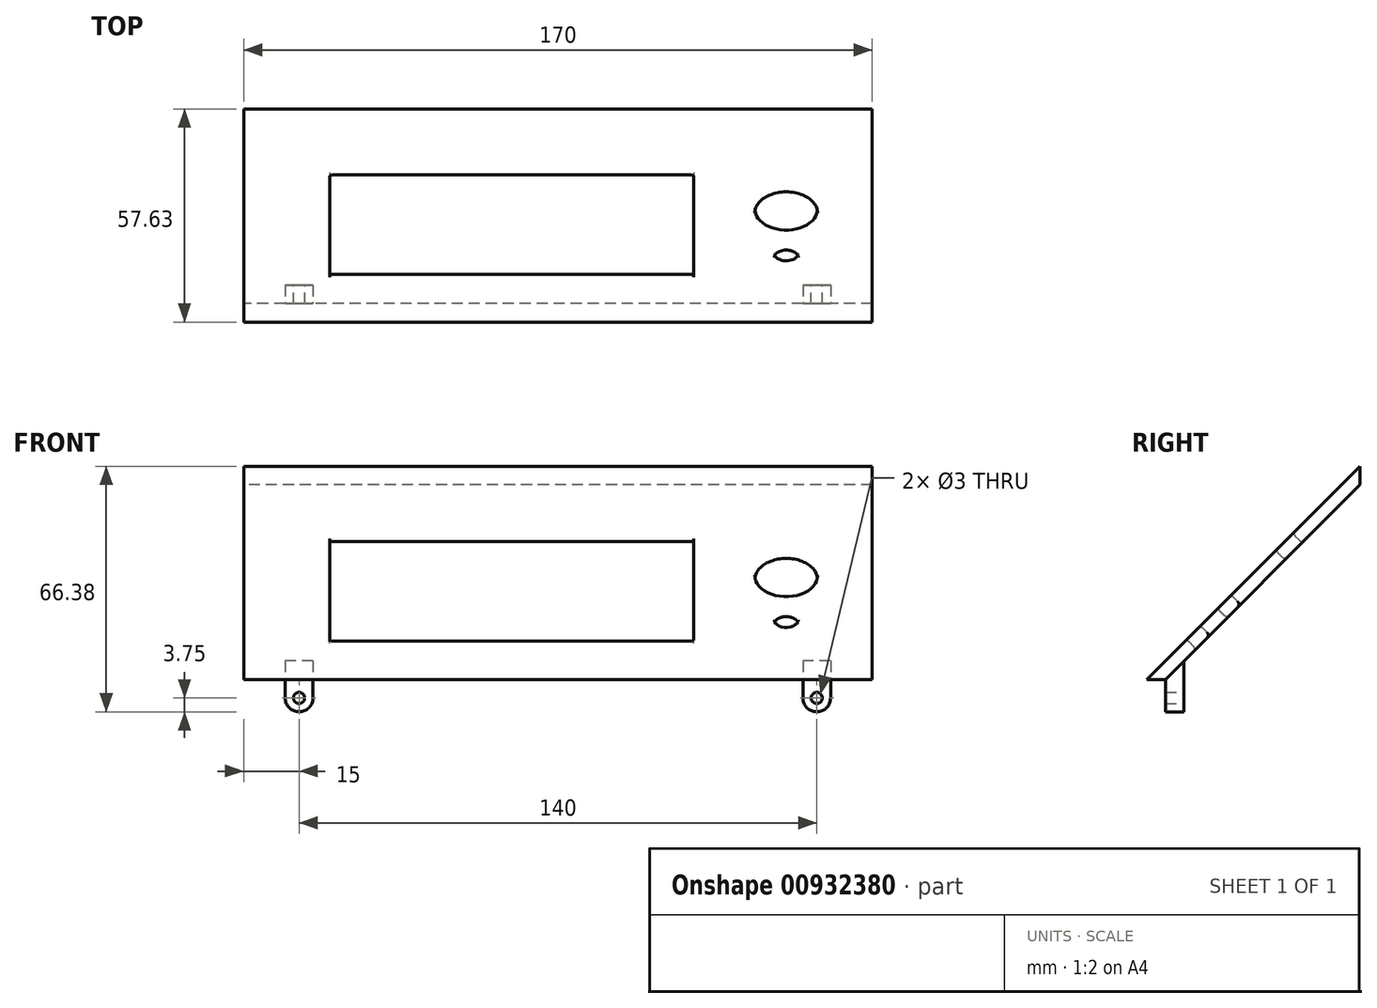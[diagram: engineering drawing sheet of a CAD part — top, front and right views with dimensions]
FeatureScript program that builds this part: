
annotation { "Feature Type Name" : "Feature", "Feature Type Description" : "" }
export const myFeature = defineFeature(function(context is Context, id is Id, definition is map)
    precondition{}
    {
        {
            var Q0;
            Q0=qCreatedBy(makeId("Right.planeOp"),FACE);
            var sketch = newSketch(context, id + "F0", { "sketchPlane" : qUnion([Q0])});
            skLineSegment(sketch, "E0", {"start": v(0, 0) * mm, "end": v(0, 57.63) * mm});
            skLineSegment(sketch, "E1", {"start": v(0, 57.63) * mm, "end": v(57.63, 57.63) * mm});
            skLineSegment(sketch, "E2", {"start": v(57.63, 57.63) * mm, "end": v(0, 0) * mm});
            skLineSegment(sketch, "E3", {"start": v(57.63, 57.63) * mm, "end": v(57.63, 52.63) * mm});
            skLineSegment(sketch, "E4", {"start": v(57.63, 52.63) * mm, "end": v(5, 0) * mm});
            skLineSegment(sketch, "E5", {"start": v(5, 0) * mm, "end": v(0, 0) * mm});
            skSolve(sketch);
        }
        {
            var Q0;
            Q0=makeQuery(id+"F0.imprint","IMPRINT",FACE,{"disambiguationData":[TD([[makeQuery(id+"F0.imprint","IMPRINT",EDGE,{"derivedFrom":sQuery(id+"F0.wireOp",EDGE,"E2")}),1.0]])]});
            extrude(context, id + "F1", {"entities" : qUnion([Q0]), "depth" : 85 * mm, "offsetDistance" : 25 * mm, "hasSecondDirection" : true, "secondDirectionOppositeDirection" : true, "secondDirectionDepth" : 85 * mm});
        }
        {
            var Q0;
            Q0=makeQuery(id+"F1.opExtrude","SWEPT_FACE",FACE,{"disambiguationData":[OSD([sQuery(id+"F0.wireOp",EDGE,"E2")])]});
            var sketch = newSketch(context, id + "F2", { "sketchPlane" : qUnion([Q0])});
            skLineSegment(sketch, "E6.bottom", {"start": v(-61.75, 55.75) * mm, "end": v(36.75, 55.75) * mm});
            skLineSegment(sketch, "E6.top", {"start": v(-61.75, 15.25) * mm, "end": v(36.75, 15.25) * mm});
            skLineSegment(sketch, "E6.left", {"start": v(-61.75, 55.75) * mm, "end": v(-61.75, 15.25) * mm});
            skLineSegment(sketch, "E6.right", {"start": v(36.75, 55.75) * mm, "end": v(36.75, 15.25) * mm});
            skCircle(sketch, "E7", {"center": v(61.75, 40.75) * mm, "radius": 8.5 * mm});
            skCircle(sketch, "E8", {"center": v(61.75, 23.75) * mm, "radius": 3.25 * mm});
            skLineSegment(sketch, "E9", {"start": v(-85, 40.75) * mm, "end": v(85, 40.75) * mm, "construction": true});
            skSolve(sketch);
        }
        {
            var Q0;
            Q0 = qSketchRegion(id + "F2", true);
            extrude(context, id + "F3", {"entities" : qUnion([Q0]), "operationType" : NewBodyOperationType.REMOVE, "endBound" : BoundingType.THROUGH_ALL, "oppositeDirection" : true, "depth" : 25 * mm, "offsetDistance" : 25 * mm});
        }
        {
            var Q0;
            Q0=qCreatedBy(makeId("Front.planeOp"),FACE);
            cPlane(context, id + "F4", {"entities" : qUnion([Q0]), "cplaneType" : CPlaneType.OFFSET, "offset" : 10 * mm, "oppositeDirection" : true, "width" : 150 * mm, "height" : 150 * mm});
        }
        {
            var Q0;
            Q0=qCreatedBy(id+"F4.planeOp",FACE);
            var sketch = newSketch(context, id + "F5", { "sketchPlane" : qUnion([Q0])});
            skLineSegment(sketch, "E10.bottom", {"start": v(73.75, 10) * mm, "end": v(66.25, 10) * mm});
            skLineSegment(sketch, "E10.left", {"start": v(73.75, 10) * mm, "end": v(73.75, -5) * mm});
            skLineSegment(sketch, "E10.right", {"start": v(66.25, 10) * mm, "end": v(66.25, -5) * mm});
            skArc(sketch, "E11", {"start": v(66.25, -5) * mm, "mid": v(70, -8.75) * mm, "end": v(73.75, -5) * mm});
            skCircle(sketch, "E12", {"center": v(70, -5) * mm, "radius": 1.5 * mm});
            skCircle(sketch, "E13.MirrorC", {"center": v(-70, -5) * mm, "radius": 1.5 * mm});
            skLineSegment(sketch, "E14.MirrorCS", {"start": v(-73.75, 10) * mm, "end": v(-73.75, -5) * mm});
            skLineSegment(sketch, "E15.MirrorCS", {"start": v(-66.25, 10) * mm, "end": v(-66.25, -5) * mm});
            skLineSegment(sketch, "E16.MirrorCS", {"start": v(-73.75, 10) * mm, "end": v(-66.25, 10) * mm});
            skArc(sketch, "E17.MirrorCS", {"start": v(-66.25, -5) * mm, "mid": v(-70, -8.75) * mm, "end": v(-73.75, -5) * mm});
            skSolve(sketch);
        }
        {
            var Q0;
            Q0 = qSketchRegion(id + "F5", true);
            var Q1;
            Q1=makeQuery(id+"F1.opExtrude","SWEPT_FACE",FACE,{"disambiguationData":[OSD([sQuery(id+"F0.wireOp",EDGE,"E4")])]});
            extrude(context, id + "F6", {"entities" : qUnion([Q0]), "operationType" : NewBodyOperationType.ADD, "depth" : 5 * mm, "endBoundEntityFace" : qUnion([Q1]), "offsetDistance" : 25 * mm});
        }
        {
            var Q0;
            Q0=makeQuery(id+"F2.imprint","IMPRINT",FACE,{"disambiguationData":[TD([[makeQuery(id+"F2.imprint","IMPRINT",EDGE,{"derivedFrom":sQuery(id+"F2.wireOp",EDGE,"E6.bottom")}),1.0]])]});
            var Q1;
            Q1=sQuery(id+"F2.wireOp",EDGE,"E9");
            cPlane(context, id + "F7", {"entities" : qUnion([Q0, Q1]), "cplaneType" : CPlaneType.LINE_ANGLE, "offset" : 25 * mm, "angle" : 90 * degree, "width" : 150 * mm, "height" : 150 * mm});
        }
        {
            var Q0;
            Q0=makeQuery(id+"F0.imprint","IMPRINT",FACE,{"disambiguationData":[TD([[makeQuery(id+"F0.imprint","IMPRINT",EDGE,{"derivedFrom":sQuery(id+"F0.wireOp",EDGE,"E0")}),-1.0]])]});
            extrude(context, id + "F8", {"entities" : qUnion([Q0]), "operationType" : NewBodyOperationType.REMOVE, "endBound" : BoundingType.THROUGH_ALL, "oppositeDirection" : true, "depth" : 25 * mm, "offsetDistance" : 25 * mm, "hasSecondDirection" : true, "secondDirectionBound" : BoundingType.THROUGH_ALL, "secondDirectionOppositeDirection" : false, "secondDirectionDepth" : 25 * mm});
        }
        {
            var Q0;
            Q0=makeQuery(id+"F3.boolean.opBoolean","COPY",FACE,{"derivedFrom":makeQuery(id+"F3.opExtrude","SWEPT_FACE",FACE,{"disambiguationData":[OSD([sQuery(id+"F2.wireOp",EDGE,"E6.bottom")])]})});
            var Q1;
            Q1=makeQuery(id+"F3.boolean.opBoolean","COPY",FACE,{"derivedFrom":makeQuery(id+"F3.opExtrude","SWEPT_FACE",FACE,{"disambiguationData":[OSD([sQuery(id+"F2.wireOp",EDGE,"E6.left")])]})});
            var Q2;
            Q2=makeQuery(id+"F3.boolean.opBoolean","COPY",FACE,{"derivedFrom":makeQuery(id+"F3.opExtrude","SWEPT_FACE",FACE,{"disambiguationData":[OSD([sQuery(id+"F2.wireOp",EDGE,"E6.right")])]})});
            var Q3;
            Q3=makeQuery(id+"F3.boolean.opBoolean","COPY",FACE,{"derivedFrom":makeQuery(id+"F3.opExtrude","SWEPT_FACE",FACE,{"disambiguationData":[OSD([sQuery(id+"F2.wireOp",EDGE,"E6.top")])]})});
            var Q4;
            Q4=makeQuery(id+"F3.boolean.opBoolean","COPY",FACE,{"derivedFrom":makeQuery(id+"F3.opExtrude","SWEPT_FACE",FACE,{"disambiguationData":[OSD([sQuery(id+"F2.wireOp",EDGE,"E7")])]})});
            var Q5;
            Q5=makeQuery(id+"F3.boolean.opBoolean","COPY",FACE,{"derivedFrom":makeQuery(id+"F3.opExtrude","SWEPT_FACE",FACE,{"disambiguationData":[OSD([sQuery(id+"F2.wireOp",EDGE,"E8")])]})});
            fillet(context, id + "F9", {"entities" : qUnion([Q0, Q1, Q2, Q3, Q4, Q5]), "radius" : 1 * mm, "tangentPropagation" : true, "allowEdgeOverflow" : false});
        }
    });
